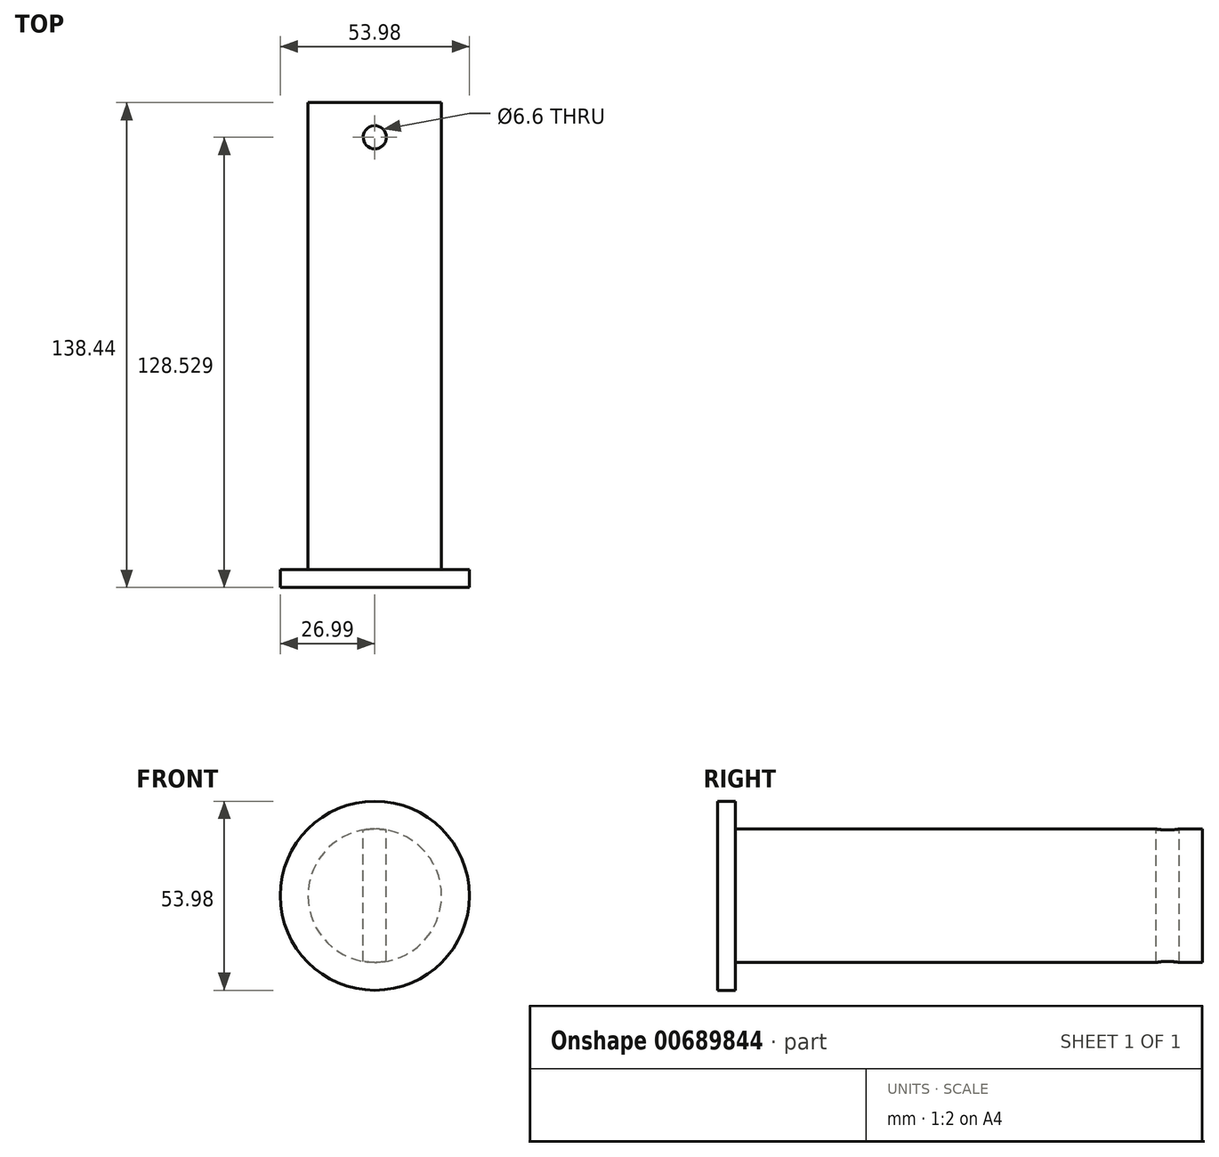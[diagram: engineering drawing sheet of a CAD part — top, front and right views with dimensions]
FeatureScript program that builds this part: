
annotation { "Feature Type Name" : "Feature", "Feature Type Description" : "" }
export const myFeature = defineFeature(function(context is Context, id is Id, definition is map)
    precondition{}
    {
        {
            var Q0;
            Q0=qCreatedBy(makeId("Front.planeOp"),FACE);
            var sketch = newSketch(context, id + "F0", { "sketchPlane" : qUnion([Q0])});
            skCircle(sketch, "E0", {"center": v(0, 0) * mm, "radius": 19.05 * mm});
            skSolve(sketch);
        }
        {
            var Q0;
            Q0 = qSketchRegion(id + "F0", true);
            extrude(context, id + "F1", {"entities" : qUnion([Q0]), "endBound" : BoundingType.SYMMETRIC, "depth" : 133.35 * mm, "offsetDistance" : 25.4 * mm});
        }
        {
            var Q0;
            Q0=makeQuery(id+"F1.opExtrude","CAP_FACE",FACE,{"disambiguationData":[OSD([sQuery(id+"F0.wireOp",EDGE,"E0")])],"isStart":false});
            var sketch = newSketch(context, id + "F2", { "sketchPlane" : qUnion([Q0])});
            skCircle(sketch, "E1", {"center": v(0, 0) * mm, "radius": 26.99 * mm});
            skSolve(sketch);
        }
        {
            var Q0;
            Q0 = qSketchRegion(id + "F2", true);
            extrude(context, id + "F3", {"entities" : qUnion([Q0]), "operationType" : NewBodyOperationType.ADD, "depth" : 5.08 * mm, "offsetDistance" : 25.4 * mm});
        }
        {
            var Q0;
            Q0=qCreatedBy(makeId("Top.planeOp"),FACE);
            var sketch = newSketch(context, id + "F4", { "sketchPlane" : qUnion([Q0])});
            skCircle(sketch, "E2", {"center": v(0, 56.77) * mm, "radius": 3.3 * mm});
            skSolve(sketch);
        }
        {
            var Q0;
            Q0 = qSketchRegion(id + "F4", true);
            extrude(context, id + "F5", {"entities" : qUnion([Q0]), "operationType" : NewBodyOperationType.REMOVE, "endBound" : BoundingType.SYMMETRIC, "oppositeDirection" : true, "depth" : 76.2 * mm, "offsetDistance" : 25.4 * mm});
        }
    });
